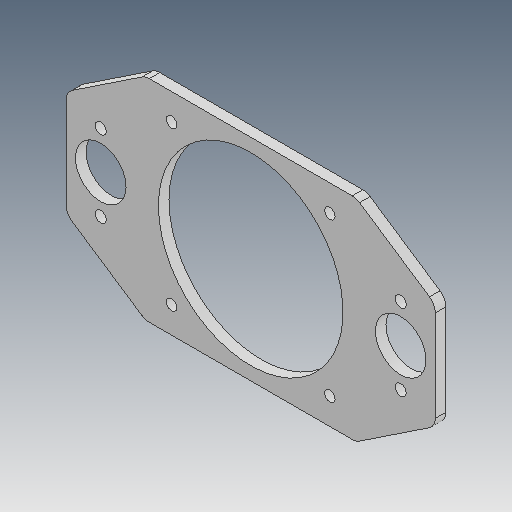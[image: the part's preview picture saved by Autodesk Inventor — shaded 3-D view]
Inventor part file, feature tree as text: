
AUTODESK INVENTOR PART (.ipt)
format: ipt  version: 2020 (Build 240168000, 168)  size: 180,224 bytes
history: native  units: mm
features: other x4, mirror x2, extrude x1, fillet x1, sketch x1
ambient origin geometry x8: Origin, YZ Plane, XZ Plane, XY Plane, X Axis, Y Axis, Z Axis, Center Point
bodies: Body1 (feature_tree)
feature tree (9):
  other  "Plano de trabalho1"
  extrude  "Extrusão2"  Depth=4.0mm
  mirror  "Espelhamento1"
  mirror  "Espelhamento2"
  fillet  "Arredondamento1"  Radius=4.0mm
  sketch  "Esboço1"  dims[d0=70.0mm d3=4.0mm d4=4.0mm d5=4.0mm d6=4.0mm d7=19.2mm d8=30.0mm d9=20.0mm d10=4.0mm d11=0.0mm d12=4.2mm d13=14.5mm d14=16.87302mm d15=16.87302mm d16=5.0mm]
  other  "<userpath>\OneDrive\Área de Trabalho\Calorimetro 2022\Inventor\parte_superior.iam"
  other  "parte_superior.iam"
  other  "Corpo_1:4"
